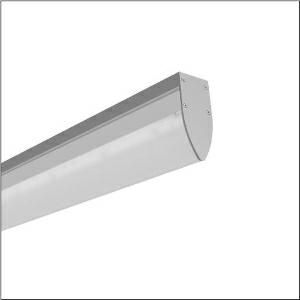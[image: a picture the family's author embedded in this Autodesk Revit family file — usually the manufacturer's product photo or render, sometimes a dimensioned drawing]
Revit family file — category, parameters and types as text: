
# Revit family: mira_r__21_td_51fr527g454a_bdf0
name_source: partatom
category: Lighting Fixtures
units: mm (PartAtom-declared; Revit-internal decimal feet)

## family parameters
Cut with Voids When Loaded = No
Host = Face
Light Source = No
Part Type = Normal
Room Calculation Point = No
Round Connector Dimension = Use Diameter
Shared = No

## types (1)
- Mira® 21 TD (1 x LED, 5500 lm, 39 W, 4000K)
    Apparent Load = 39 VA
    CIE Flux Codes = 40 68 87 81 100
    Color Rendering = 80
    Color Temperature = 4000K
    Default Elevation = 1800 mm
    Description = Mira® 21 TD, clean room luminaire, primary light control with reflector, primary optical cover: cover, of PMMA, frosted, light emission: direct distribution, primary light characteristic: symmetric, installation type: surface-mounted, LED, rated luminous flux: 5.500lm, luminous efficacy: 141lm/W, light colour: 840, colour temperature: 4000K, control gear: ON/OFF, with terminal, 3-pole, max. 2.5mm², mains connection: 230V, AC, 50/60Hz, rated input power: 39W, luminaire housing, of sheet steel, coated, pure white (RAL 9010), length: 900mm, width: 55mm, height: 120mm, protection rating (complete): IP43, insulation class (complete): insulation class I (protective earthing), certification: CE, UKCA, permissible operating ambient temperature: -5..+40°C, standard: EN 50419, packaging unit: 1 piece
    Height = 120 mm
    Lamp = 1 x LED
    Lamp Light Flux = 5500 lm
    Lamp Power = 39 W
    Lamp count = 1
    Length = 900 mm
    Luminous efficacy = 141 lm/W
    Manufacturer = Siteco
    ModVariant = No
    Model = 51FR527G454A
    Mounting Place = Ceiling
    Mounting Type = Surface mounted
    Number of Poles = 1
    OnlyDefault = Yes
    Power Factor = 1
    Product Name = Mira® 21 TD
    Product group = clean room luminaire | ceiling mounted
    ProductGroupID = 305
    Protection Class = Protection class I
    Protection Degree = IP 43
    RLX_Detail_Level = 1
    RLX_Emergency_Light_Flux = 0 lm
    RLX_Emergency_Type = 0
    RLX_Emergency_Type_DB = No
    RlxData = <blob elided: 25137 chars, md5=b750e3ba>
    Socket = socket
    Standby Power = 0 W
    System Light Flux = 5500 lm
    System Power = 39 W
    Type Comments = Product without accessories
    Type Image = l_1007115.jpg
    URL = http://relux.com
    VarID = ---
    Voltage = 0 V
    Weight = 0.00 kg
    Width = 55 mm

## geometry (parser evidence)
native form markers: Blend x4, Sweep x12
no freeform markers — native parametric forms only
